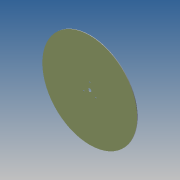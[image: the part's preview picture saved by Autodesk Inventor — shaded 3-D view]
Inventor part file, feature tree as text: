
AUTODESK INVENTOR PART (.ipt)
format: ipt  version: 2013 SP2 (Build 170200200, 200)  size: 96,768 bytes
history: native  units: in
note: dims shown in document units (in); Inventor stores cm internally (conversion verified against a paired STEP export)
features: other x2, sketch x2, extrude x1, hole x1, pattern_circular x1, imported_body x1
ambient origin geometry x8: Origin, YZ Plane, XZ Plane, XY Plane, X Axis, Y Axis, Z Axis, Center Point
feature tree (8):
  other  "TopDisk"
  other  "TopDisk1"
  extrude  "Extrusion1"  Depth=0.3937in TaperAngle=0.0deg
  hole  "Hole2"  [1 undecoded]
  pattern_circular  "Circular Pattern1"  [2 undecoded]
  imported_body  "Base1"
  sketch  "Sketch1"  dims[d0=0.7874in d2=0.3937in d3=0.0in]
  sketch  "Sketch3"  dims[d12=1.75in d13=0.266in d14=0.2356in d15=0.507in d16=0.0787in d17=0.5635in d18=0.315in d19=0.8108in d20=1.1811in d21=360.0deg]
note: 3 required parameter values undecoded (feature->parameter linkage not recoverable at this tier; creation-order binding heuristic only, values carry confidence <= 0.55)
